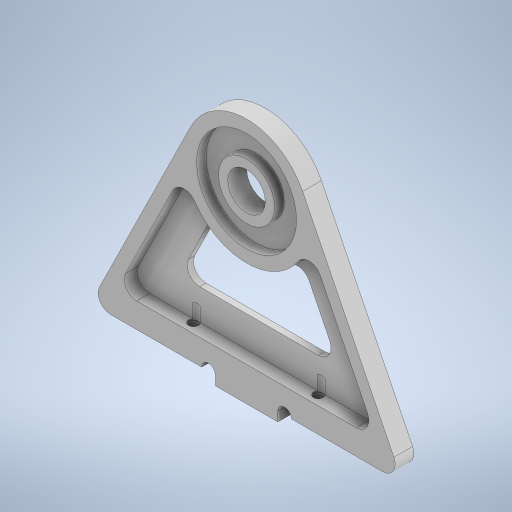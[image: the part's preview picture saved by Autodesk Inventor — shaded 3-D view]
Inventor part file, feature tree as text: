
AUTODESK INVENTOR PART (.ipt)
format: ipt  version: 2024 (Build 280153000, 153)  size: 367,616 bytes
history: native  units: mm
features: extrude x4, sketch x4, fillet x3, other x1, hole x1, projected_geometry x1
ambient origin geometry x8: Origin, YZ Plane, XZ Plane, XY Plane, X Axis, Y Axis, Z Axis, Center Point
bodies: Body1 (feature_tree)
feature tree (14):
  other  "ソリッド1"
  extrude  "押し出し1"  Depth=6.0mm
  fillet  "フィレット1"  Radius=20.0mm
  hole  "穴1"  [1 undecoded]
  sketch  "スケッチ3"
  extrude  "押し出し2"  Depth=1.5mm
  fillet  "フィレット2"  Radius=10.0mm
  extrude  "押し出し3"  Depth=2.2mm
  extrude  "押し出し4"  Depth=2.2mm
  fillet  "フィレット3"  Radius=50.0mm
  sketch  "スケッチ1"
  sketch  "スケッチ2"
  projected_geometry  "投影ループ1"
  sketch  "スケッチ4"
note: 1 required parameter value undecoded (feature->parameter linkage not recoverable at this tier; creation-order binding heuristic only, values carry confidence <= 0.55)
